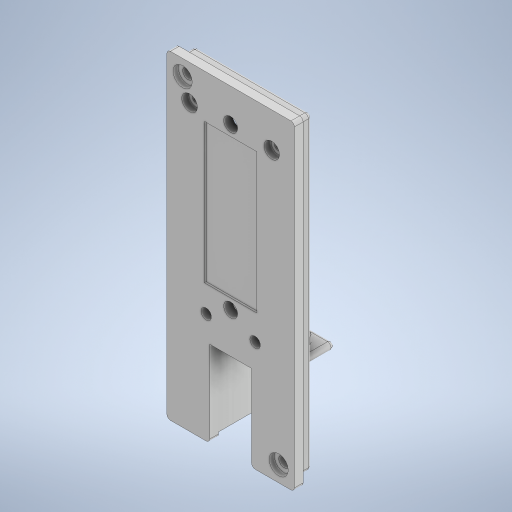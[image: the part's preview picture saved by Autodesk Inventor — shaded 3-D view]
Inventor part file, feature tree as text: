
AUTODESK INVENTOR PART (.ipt)
format: ipt  version: 2024 (Build 280153000, 153)  size: 569,344 bytes
history: native  units: mm
features: extrude x23, sketch x23, fillet x7
ambient origin geometry x8: Origin, YZ Plane, XZ Plane, XY Plane, X Axis, Y Axis, Z Axis, Center Point
bodies: Volumenkörper1 (feature_tree)
feature tree (53):
  extrude  "Extrusion1"  Depth=36.5mm
  extrude  "Extrusion2"  Depth=1.5mm
  extrude  "Extrusion3"  Depth=1.5mm
  extrude  "Extrusion7"  Depth=4.0mm TaperAngle=0.0deg
  extrude  "Extrusion9"  Depth=1.5mm
  extrude  "Extrusion10"  Depth=1.5mm
  extrude  "Extrusion11"  Depth=60.0mm
  extrude  "Extrusion12"  Depth=12.0mm TaperAngle=0.0deg
  extrude  "Extrusion13"  Depth=4.0mm
  extrude  "Extrusion14"  Depth=1.5mm
  fillet  "Rundung4"  Radius=1.5mm
  fillet  "Rundung5"  Radius=2.0mm
  extrude  "Extrusion15"  Depth=12.0mm TaperAngle=0.0deg
  fillet  "Rundung8"  Radius=0.5mm
  extrude  "Extrusion17"  Depth=1.368mm TaperAngle=0.0deg
  extrude  "Extrusion18"  Depth=12.0mm
  extrude  "Extrusion19"  Depth=2.5mm
  extrude  "Extrusion20"  Depth=15.0mm
  extrude  "Extrusion21"  Depth=12.5mm
  extrude  "Extrusion22"  Depth=1.0mm
  fillet  "Rundung9"  Radius=1.0mm
  extrude  "Extrusion23"  Depth=4.0mm
  extrude  "Extrusion24"  Depth=4.0mm
  fillet  "Rundung10"  Radius=3.0mm
  extrude  "Extrusion26"  Depth=3.0mm
  extrude  "Extrusion27"  Depth=10.0mm TaperAngle=0.0deg
  fillet  "Rundung12"  Radius=1.0mm
  extrude  "Extrusion28"  Depth=1.5mm
  fillet  "Rundung13"  Radius=3.0mm
  extrude  "Extrusion29"  Depth=5.5mm
  sketch  "Skizze1"  dims[d0=91.5mm d1=36.5mm]
  sketch  "Skizze2"  dims[d2=2.5mm d3=0.0mm d4=1.5mm]
  sketch  "Skizze3"  dims[d5=1.5mm d6=1.5mm]
  sketch  "Skizze7"  dims[d7=1.5mm d8=4.0mm d9=0.0mm]
  sketch  "Skizze9"  dims[d10=1.5mm d11=1.5mm]
  sketch  "Skizze11"  dims[d12=1.5mm d13=1.5mm]
  sketch  "Skizze12"  dims[d14=4.0mm d15=0.0mm d29=60.0mm]
  sketch  "Skizze14"  dims[d30=2.0mm d31=12.0mm d32=0.0mm]
  sketch  "Skizze15"  dims[d39=17.0mm d40=4.0mm]
  sketch  "Skizze16"  dims[d41=4.0mm d42=1.5mm d43=1.5mm d44=2.0mm d45=0.0mm]
  sketch  "Skizze17"  dims[d46=7.3mm d47=12.0mm d48=0.0mm d49=0.5mm]
  sketch  "Skizze18"  dims[d50=0.5mm d51=1.368mm d52=0.0mm]
  sketch  "Skizze19"  dims[d53=12.0mm d54=12.0mm]
  sketch  "Skizze20"  dims[d55=24.5mm d56=0.0mm d57=2.5mm]
  sketch  "Skizze21"  dims[d58=7.5mm d59=0.0mm d60=15.0mm]
  sketch  "Skizze22"  dims[d61=40.0mm d62=12.5mm]
  sketch  "Skizze23"  dims[d63=0.5mm d64=0.0mm d68=1.0mm d69=1.0mm]
  sketch  "Skizze24"  dims[d72=2.5mm d73=4.0mm]
  sketch  "Skizze25"  dims[d74=2.5mm d75=4.0mm d76=3.0mm]
  sketch  "Skizze26"  dims[d77=4.0mm d78=3.0mm]
  sketch  "Skizze27"  dims[d79=4.0mm d80=10.0mm d81=0.0mm d82=1.0mm]
  sketch  "Skizze28"  dims[d83=1.5mm d84=1.5mm d85=3.0mm]
  sketch  "Skizze29"  dims[d88=12.0mm d89=0.0mm d90=5.5mm d91=1.5mm d92=0.0mm d93=1.5mm d94=1.5mm d95=3.0mm d96=2.0mm d97=0.0mm d98=5.5mm d99=1.5mm d100=0.0mm d101=4.0mm d102=4.0mm d103=4.0mm d104=0.0mm d105=3.0mm d106=12.0mm d107=0.0mm d108=2.0mm d109=4.0mm d110=4.0mm d111=4.0mm d112=0.0mm d113=3.0mm d114=10.0mm d115=0.0mm d116=2.0mm d117=7.0mm d118=3.5mm d119=2.5mm d122=7.0mm d123=3.5mm d124=2.5mm d125=6.0mm d126=0.0mm d127=4.5mm d128=4.5mm d129=2.0mm d130=0.0mm d132=6.0mm d133=2.0mm d134=1.65mm d135=1.65mm d136=1.5mm d137=1.5mm d138=4.0mm d139=4.0mm d140=2.0mm d141=0.0mm d142=2.0mm d143=3.0mm d144=7.0mm d145=7.0mm d146=3.0mm d147=3.0mm d148=10.0mm d149=0.0mm d120=0.5mm d121=0.872665mm]
